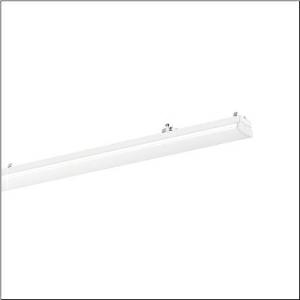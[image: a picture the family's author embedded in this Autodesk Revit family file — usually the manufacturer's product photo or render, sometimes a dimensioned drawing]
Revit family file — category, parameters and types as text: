
# Revit family: licross_r__21_recessed_opal_mo_52tl1ddv495g_d7bc
name_source: partatom
category: Lighting Fixtures
units: mm (PartAtom-declared; Revit-internal decimal feet)

## family parameters
Cut with Voids When Loaded = No
Host = Face
Light Source = No
Part Type = Normal
Room Calculation Point = No
Round Connector Dimension = Use Diameter
Shared = No

## types (1)
- --- (1 x LED, 9500 lm, 53.6 W, 4000K)
    Apparent Load = 54 VA
    CIE Flux Codes = 44 73 91 87 100
    Color Rendering = 80
    Color Temperature = 4000K
    Default Elevation = 1800 mm
    Description = Licross® 21 recessed opal MO, luminaire insert, of sheet steel, galvanised, coil coated, white, length: 2.250mm, width: 66mm, height: 67mm, LED rated luminous flux: 9.500lm, light colour: 840, control gear: DALI 2, with plug, 5-pole, with phase selection, mains connection: 220..240V, AC, 50/60Hz, rated input power: 54W, internal wiring halogen-free, primary optical cover: cover, of PMMA, light emission: direct with ceiling illumination distribution, primary light characteristic: symmetric, protection rating (complete): IP40, insulation class (complete): insulation class I (protective earthing), certification: CE, ENEC, VDE, UKCA, protection symbol: D if used in an environment without relevant dust loads with corresponding accessories, impact resistance: IK06, permissible ambient temperature for indoor applications: -25..+40°C, corresponds to IFS (International Featured Standards) requirements for safety and quality in the food industry, reducing of maximum allowable ambient temperature of 5°C with ceiling mounting, LABS conformity tested according to VDMA 24364:2018-05, packaging unit: 1 piece
    Height = 83 mm
    Lamp = 1 x LED
    Lamp Light Flux = 9500 lm
    Lamp Power = 53.6 W
    Lamp count = 1
    Length = 2250 mm
    Luminous efficacy = 177 lm/W
    Manufacturer = Siteco
    ModVariant = No
    Model = 52TL1DDV495G
    Mounting Place = Ceiling
    Mounting Type = Pendant
    Number of Poles = 1
    OnlyDefault = Yes
    Power Factor = 1
    Product Name = Licross® 21 recessed opal MO
    Product group = luminaire insert | ceiling pendant
    ProductGroupID = 902
    Protection Class = Protection class I
    Protection Degree = IP 40
    RLX_Detail_Level = 1
    RLX_Emergency_Light_Flux = 0 lm
    RLX_Emergency_Type = 0
    RLX_Emergency_Type_DB = No
    RlxData = <blob elided: 26501 chars, md5=f0e640db>
    Socket = socket
    Standby Power = 0 W
    System Light Flux = 9500 lm
    System Power = 54 W
    Type Comments = factory setting: luminous flux: 100 % | dim-lin: 254 | 246 mA
    Type Image = l_1313666.jpg
    URL = http://relux.com
    VarID = @adj_086123
    Voltage = 0 V
    Weight = 0.00 kg
    Width = 76 mm

## geometry (parser evidence)
native form markers: Blend x4, Sweep x13
no freeform markers — native parametric forms only
